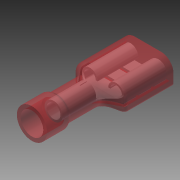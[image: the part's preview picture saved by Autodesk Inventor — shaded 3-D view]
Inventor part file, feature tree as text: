
AUTODESK INVENTOR PART (.ipt)
format: ipt  version: 2014 (Build 180170000, 170)  size: 741,888 bytes
history: native  units: in
note: dims shown in document units (in); Inventor stores cm internally (conversion verified against a paired STEP export)
features: sketch x17, projected_geometry x12, extrude x11, fillet x5, plane x5, loft x3, shell x1, revolve x1, mirror x1, chamfer x1, other x1
ambient origin geometry x8: Origin, YZ Plane, XZ Plane, XY Plane, X Axis, Y Axis, Z Axis, Center Point
bodies: Solid1 (feature_tree), Solid2 (feature_tree)
feature tree (58):
  extrude  "Extrusion1"  Depth=0.381in TaperAngle=0.0deg
  extrude  "Extrusion2"  Depth=0.16in TaperAngle=0.0deg
  fillet  "Fillet1"  Radius=0.02in
  fillet  "Fillet2"  Radius=0.03in
  shell  "Shell1"  Thickness=0.026in
  revolve  "Revolution1"  Angle=90.0deg
  plane  "Work Plane1"
  plane  "Work Plane2"
  extrude  "Extrusion3"  Depth=0.2905in
  mirror  "Mirror1"
  loft  "Loft2"
  fillet  "Fillet3"  Radius=0.109in
  chamfer  "Chamfer1"  Distance=0.291in
  extrude  "Extrusion4"  Depth=0.003in TaperAngle=45.0deg
  extrude  "Extrusion5"  Depth=0.3937in TaperAngle=90.0deg
  fillet  "Fillet4"  Radius=0.015in
  extrude  "Extrusion6"  Depth=0.015in TaperAngle=0.0deg
  extrude  "Extrusion7"  Depth=0.0235in
  extrude  "Extrusion8"  Depth=0.003in TaperAngle=0.0deg
  fillet  "Fillet5"  Radius=0.003in
  plane  "Work Plane3"
  extrude  "Extrusion9"  Depth=0.01in
  extrude  "Extrusion10"  Depth=0.005in
  plane  "Work Plane4"
  plane  "Work Plane5"
  extrude  "Extrusion11"  Depth=0.02in
  sketch  "Sketch19"  dims[d56=0.02in d57=0.01in]
  sketch  "Sketch20"  dims[d58=0.01in d59=0.01in]
  sketch  "Sketch21"  dims[d60=0.02in d61=0.02in d62=0.01in d63=0.3125in d64=0.0in d70=90.0deg d71=0.3937in d72=90.0deg d73=0.3937in d74=0.0in d75=90.0deg d76=0.0in d77=90.0deg]
  loft  "Loft3"
  loft  "Loft4"
  sketch  "Sketch1"  dims[d0=0.1755in d1=0.381in d2=0.0in]
  sketch  "Sketch2"  dims[d3=0.208in d4=0.16in d5=0.0in d6=0.02in d7=0.03in d8=0.026in]
  projected_geometry  "Projected Loop1"
  sketch  "Sketch3"  dims[d9=0.014in d10=90.0deg]
  sketch  "Sketch5"  dims[d11=0.4in d12=0.2905in]
  sketch  "Sketch6"  dims[d13=0.0135in d14=0.037in d15=0.109in]
  projected_geometry  "Projected Loop2"
  sketch  "Sketch7"  dims[d16=0.01in d17=0.291in d18=0.0in]
  projected_geometry  "Projected Loop3"
  sketch  "Sketch8"  dims[d23=0.03in d24=0.003in d25=0.125in d26=45.0deg]
  projected_geometry  "Projected Loop4"
  sketch  "Sketch9"  dims[d27=0.0in d28=90.0deg d29=0.3937in d30=90.0deg d31=0.015in]
  projected_geometry  "Projected Loop5"
  sketch  "Sketch10"  dims[d32=0.291in d33=0.0in d34=0.015in d35=0.0in]
  projected_geometry  "Projected Loop6"
  sketch  "Sketch11"  dims[d36=0.005in d37=0.0235in]
  projected_geometry  "Projected Loop7"
  sketch  "Sketch12"  dims[d38=0.014in d39=0.0in d40=0.003in d41=0.0in d42=0.003in d43=0.0in]
  sketch  "Sketch14"  dims[d44=0.005in d45=0.01in]
  sketch  "Sketch15"  dims[d46=0.003in d47=0.0in d48=0.005in]
  projected_geometry  "Projected Loop8"
  sketch  "Sketch17"  dims[d49=0.05in d50=0.0in d51=0.02in]
  projected_geometry  "Projected Loop10"
  projected_geometry  "Projected Loop11"
  projected_geometry  "Projected Loop12"
  other  "Edges1"
  projected_geometry  "Project Cut Edges1"
